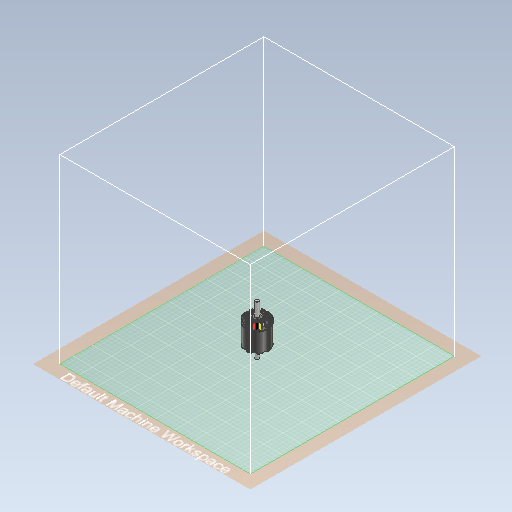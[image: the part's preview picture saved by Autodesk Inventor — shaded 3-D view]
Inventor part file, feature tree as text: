
AUTODESK INVENTOR PART (.ipt)
format: ipt  version: 2020.3 (Build 243373000, 373)  size: 2,648,576 bytes
history: native  units: mm
features: fillet x13, pattern_circular x12, extrude x10, sketch x7, revolve x1, chamfer x1, projected_geometry x1
ambient origin geometry x8: Origin, YZ Plane, XZ Plane, XY Plane, X Axis, Y Axis, Z Axis, Center Point
bodies: Solid1 (feature_tree)
feature tree (45):
  revolve  "Revolution1"  [1 undecoded]
  sketch  "Sketch2"  dims[d18=4.0mm d19=4.0mm]
  extrude  "Extrusion1"  Depth=4.0mm
  pattern_circular  "Circular Pattern1"  Count=2 Angle=90.0deg
  pattern_circular  "Circular Pattern2"  Count=2  [1 undecoded]
  extrude  "Extrusion2"  Depth=40.0mm TaperAngle=360.0deg
  pattern_circular  "Circular Pattern3"  Count=3 Angle=180.0deg
  extrude  "Extrusion3"  Depth=0.2mm TaperAngle=0.0deg
  pattern_circular  "Circular Pattern4"  Count=2 Angle=90.0deg
  pattern_circular  "Circular Pattern5"  Count=2  [1 undecoded]
  extrude  "Extrusion4"  Depth=0.2mm
  pattern_circular  "Circular Pattern6"  [2 undecoded]
  pattern_circular  "Circular Pattern7"  [2 undecoded]
  extrude  "Extrusion5"  Depth=0.2mm
  sketch  "Sketch4"  dims[d23=7.0mm d24=0.0mm d25=20.0mm d26=90.0deg d28=20.0mm d29=-15.707963mm]
  extrude  "Extrusion6"  Depth=0.2mm
  extrude  "Extrusion7"  Depth=0.2mm
  extrude  "Extrusion8"  Depth=0.2mm
  chamfer  "Chamfer1"  Distance=2.8mm
  extrude  "Extrusion9"  Depth=0.2mm TaperAngle=0.0deg
  pattern_circular  "Circular Pattern8"  [2 undecoded]
  fillet  "Fillet1"  Radius=1.0mm
  pattern_circular  "Circular Pattern9"  Angle=45.0deg  [1 undecoded]
  fillet  "Fillet2"  Radius=20.0mm
  pattern_circular  "Circular Pattern10"  [2 undecoded]
  fillet  "Fillet3"  Radius=80.0mm
  fillet  "Fillet4"  Radius=0.5mm
  fillet  "Fillet5"  Radius=80.0mm
  fillet  "Fillet6"  Radius=80.0mm
  fillet  "Fillet7"  Radius=0.5mm
  pattern_circular  "Circular Pattern11"  [2 undecoded]
  fillet  "Fillet8"  Radius=0.5mm
  fillet  "Fillet9"  Radius=0.5mm
  pattern_circular  "Circular Pattern12"  Count=4 Angle=360.0deg
  fillet  "Fillet10"  Radius=0.5mm
  fillet  "Fillet11"  Radius=30.0mm
  extrude  "Extrusion10"  Depth=0.2mm
  fillet  "Fillet12"  Radius=1.0mm
  fillet  "Fillet13"  Radius=24.0mm
  sketch  "Sketch1"  dims[d15=90.0deg d17=4.0mm]
  projected_geometry  "Projected Loop1"
  sketch  "Sketch3"  dims[d20=4.0mm]
  sketch  "Sketch5"  dims[d31=7.0mm d32=0.0mm d33=40.0mm d34=360.0deg]
  sketch  "Sketch6"  dims[d36=7.0mm d37=0.0mm d38=30.0mm d39=180.0deg]
  sketch  "Sketch7"  dims[d41=20.0mm d42=-15.707963mm d44=7.0mm d45=0.0mm d46=20.0mm d47=90.0deg d49=20.0mm d50=-15.707963mm d54=4.0mm d55=7.0mm d56=0.0mm d57=4.0mm d58=2.0mm d59=4.0mm d60=2.8mm d61=2.8mm d62=2.8mm d63=20.0mm d64=0.0mm d65=22.0mm d66=0.0mm d67=1.0mm d68=0.0mm d69=2.0mm d70=1.0mm d71=45.0deg d72=20.0mm d74=22.5deg d76=8.0mm d77=0.0mm d78=80.0mm d79=360.0deg d81=0.5mm d82=80.0mm d83=360.0deg d85=0.5mm d86=80.0mm d87=360.0deg d89=0.5mm d90=0.5mm d91=0.5mm d92=0.5mm d93=0.5mm d94=40.0mm d95=360.0deg d97=0.5mm d98=0.5mm d99=30.0mm d100=180.0deg d102=0.5mm d103=0.5mm d104=1.0mm d105=24.0mm d106=0.0mm d107=0.5mm d108=0.2mm]
note: 14 required parameter values undecoded (feature->parameter linkage not recoverable at this tier; creation-order binding heuristic only, values carry confidence <= 0.55)